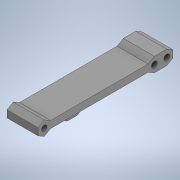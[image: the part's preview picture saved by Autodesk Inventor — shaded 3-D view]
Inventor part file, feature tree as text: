
AUTODESK INVENTOR PART (.ipt)
format: ipt  version: 2020 (Build 240168000, 168)  size: 349,184 bytes
history: native  units: in
note: dims shown in document units (in); Inventor stores cm internally (conversion verified against a paired STEP export)
features: sketch x6, extrude x5, projected_geometry x3, plane x2, mirror x1, fillet x1
ambient origin geometry x8: Origin, YZ Plane, XZ Plane, XY Plane, X Axis, Y Axis, Z Axis, Center Point
bodies: Solid1 (feature_tree)
feature tree (18):
  extrude  "Extrusion1"  Depth=3.4256in
  plane  "Work Plane1"
  extrude  "Extrusion2"  Depth=0.7874in
  sketch  "Sketch4"  dims[d4=0.0in d5=0.0827in]
  extrude  "Extrusion4"  Depth=0.0827in
  plane  "Work Plane2"
  extrude  "Extrusion6"  Depth=3.1106in
  mirror  "Mirror2"
  extrude  "Extrusion8"  Depth=0.315in
  fillet  "Fillet1"  Radius=0.1476in
  sketch  "Sketch1"  dims[d0=0.1818in d1=3.4256in]
  sketch  "Sketch2"  dims[d2=0.1378in d3=0.7874in]
  sketch  "Sketch5"  dims[d6=0.7874in d7=0.0in d28=3.1106in]
  sketch  "Sketch7"  dims[d29=0.315in d31=0.315in d33=0.1476in]
  projected_geometry  "Projected Loop7"
  projected_geometry  "Projected Loop8"
  sketch  "Sketch10"  dims[d34=0.2362in d35=0.0in d38=0.315in d39=0.2756in d40=-0.3092in d60=1.0994in d61=0.1378in d63=1.1811in d64=0.1575in d65=0.0in d66=0.126in d67=0.1575in d70=0.0984in]
  projected_geometry  "Projected Loop10"
